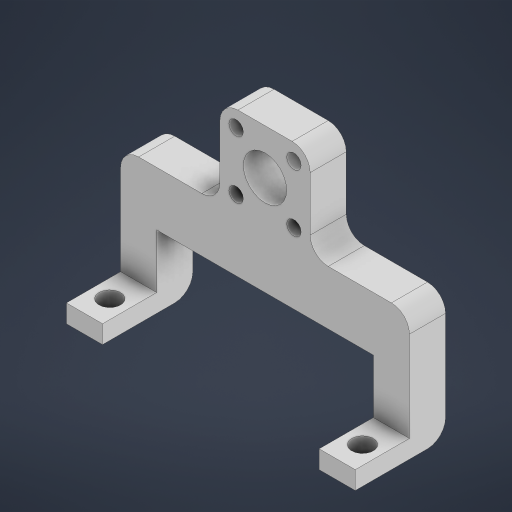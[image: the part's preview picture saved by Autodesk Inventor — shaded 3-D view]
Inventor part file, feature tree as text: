
AUTODESK INVENTOR PART (.ipt)
format: ipt  version: 2023.2 (Build 272271000, 271)  size: 258,048 bytes
history: native  units: mm
features: extrude x4, sketch x2, fillet x1
ambient origin geometry x8: Origin, YZ Plane, XZ Plane, XY Plane, X Axis, Y Axis, Z Axis, Center Point
bodies: Volumenkörper1 (feature_tree)
feature tree (7):
  sketch  "Skizze1"  dims[d0=80.0mm d1=10.0mm]
  extrude  "Extrusion1"  Depth=10.0mm
  extrude  "Extrusion2"  Depth=10.0mm
  extrude  "Extrusion3"  Depth=15.0mm
  extrude  "Extrusion4"  Depth=6.0mm
  fillet  "Rundung1"  Radius=7.0mm
  sketch  "Skizze2"  dims[d2=60.0mm d3=0.0mm d4=10.0mm d5=15.0mm d6=6.0mm d7=7.0mm d8=5.0mm d9=5.0mm d10=0.0mm d11=20.0mm d12=0.0mm d14=4.0mm d15=47.5mm d16=8.0mm d17=8.0mm d18=20.0mm d20=16.0mm d21=20.0mm d23=16.0mm d26=12.0mm d27=25.0mm d28=20.0mm d29=0.0mm d30=5.0mm]
